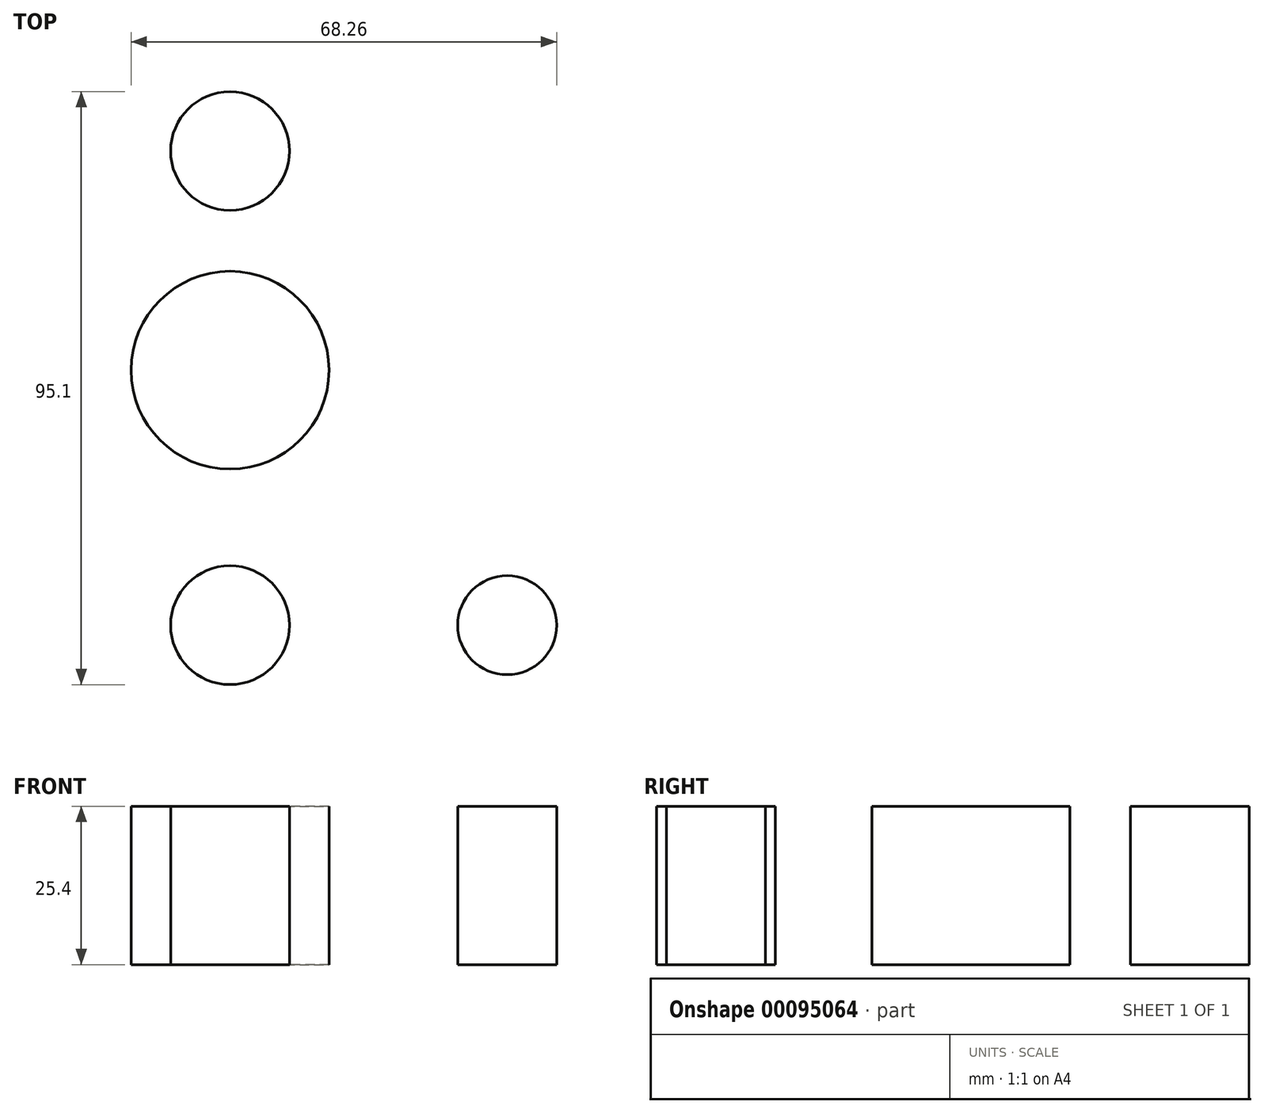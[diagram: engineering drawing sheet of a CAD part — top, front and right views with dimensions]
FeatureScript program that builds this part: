
annotation { "Feature Type Name" : "Feature", "Feature Type Description" : "" }
export const myFeature = defineFeature(function(context is Context, id is Id, definition is map)
    precondition{}
    {
        {
            var Q0;
            Q0=qCreatedBy(makeId("Top.planeOp"),FACE);
            var sketch = newSketch(context, id + "F0", { "sketchPlane" : qUnion([Q0])});
            skLineSegment(sketch, "E0", {"start": v(-41.85, 76.04) * mm, "end": v(-41.85, 0) * mm, "construction": true});
            skLineSegment(sketch, "E1", {"start": v(-41.85, 0) * mm, "end": v(2.6, 0) * mm, "construction": true});
            skCircle(sketch, "E2", {"center": v(-41.85, 76.04) * mm, "radius": 9.53 * mm});
            skCircle(sketch, "E3", {"center": v(-41.85, 40.9) * mm, "radius": 15.88 * mm});
            skCircle(sketch, "E4", {"center": v(-41.85, 0) * mm, "radius": 9.53 * mm});
            skCircle(sketch, "E5", {"center": v(2.6, 0) * mm, "radius": 7.94 * mm});
            skLineSegment(sketch, "E6", {"start": v(-51.37, 76.99) * mm, "end": v(-57.47, 43.76) * mm});
            skLineSegment(sketch, "E7", {"start": v(-32.33, 76.35) * mm, "end": v(-26.24, 43.76) * mm});
            skLineSegment(sketch, "E8", {"start": v(-57.54, 38.43) * mm, "end": v(-51.5, 0) * mm});
            skLineSegment(sketch, "E9", {"start": v(-26.17, 38.43) * mm, "end": v(-31.86, 2.21) * mm});
            skLineSegment(sketch, "E10", {"start": v(-41.9, -9.52) * mm, "end": v(2.88, -7.93) * mm});
            skLineSegment(sketch, "E11", {"start": v(-33.63, 4.8) * mm, "end": v(0, 7.74) * mm});
            skSolve(sketch);
        }
        {
            var Q0;
            Q0 = qSketchRegion(id + "F0", true);
            extrude(context, id + "F1", {"entities" : qUnion([Q0]), "depth" : 25.4 * mm});
        }
    });
